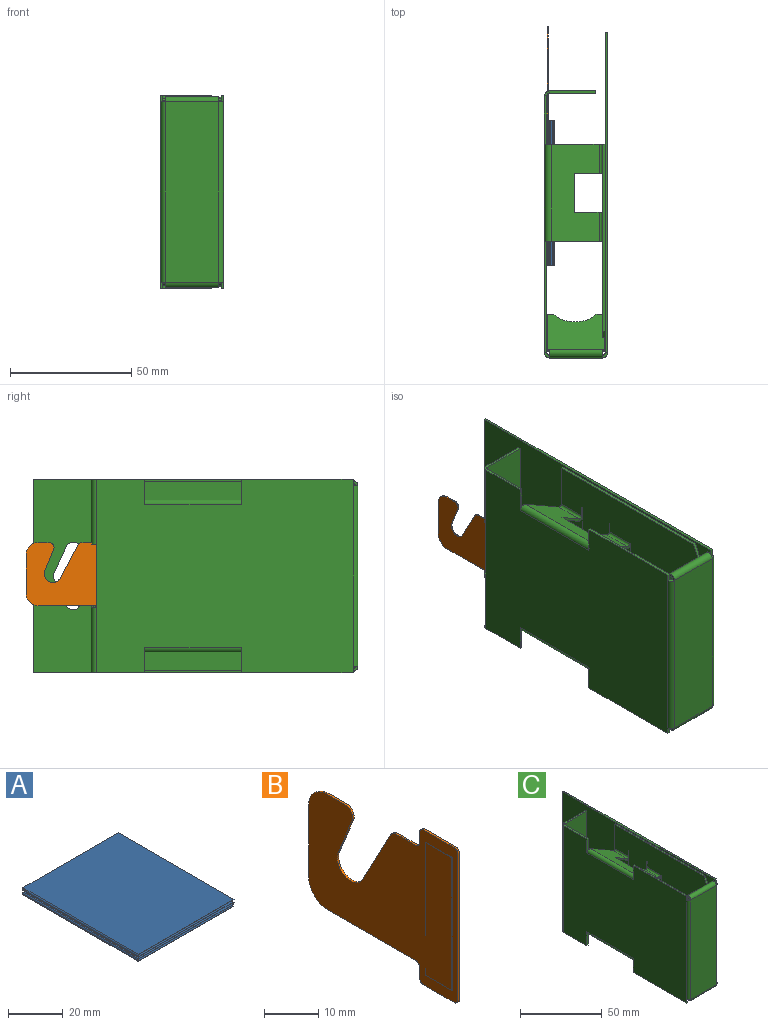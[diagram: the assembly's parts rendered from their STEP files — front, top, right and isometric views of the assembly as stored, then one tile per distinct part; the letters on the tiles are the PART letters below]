
ASSEMBLY  parts=3 mates=2
PART A: 54 faces, bbox 50x60x3.1 mm
  f0: plane 60x0.1mm, normal (1,0,0), area 6mm2, adj f1,f2,f3,f4
  f1: plane 49.5x0.1mm, normal (0,1,0), area 4.9mm2, adj f0,f3,f4,f10
  f2: plane 49.5x0.1mm, normal (0,-1,0), area 4.9mm2, adj f0,f3,f4,f9
  f3: plane 60x49.5mm, normal (0,0,1), area 2970mm2, adj f0,f1,f2,f11
  f4: plane 60x49.5mm, normal (0,0,-1), area 2970mm2, adj f0,f1,f2,f12
  f5: plane 0.1x0.1mm, normal (0,1,0), area 0mm2, adj f7,f8,f10,f14
  f6: plane 0.1x0.1mm, normal (0,-1,0), area 0mm2, adj f7,f8,f9,f13
  f7: plane 60x0.1mm, normal (-1,0,0), area 6mm2, adj f5,f6,f11,f15
  f8: plane 60x0.1mm, normal (1,0,0), area 6mm2, adj f5,f6,f12,f16
  f9: plane 0.5x0.5mm, normal (0,-1,0), area 0.1mm2, adj f2,f6,f11,f12
  f10: plane 0.5x0.5mm, normal (0,1,0), area 0.1mm2, adj f1,f5,f11,f12
  f11: cylinder r=0.5mm len=60mm, axis (0,-1,0), area 47.1mm2, adj f3,f7,f9,f10
  f12: cylinder r=0.4mm len=60mm, axis (0,-1,0), area 37.7mm2, adj f4,f8,f9,f10
  f13: plane 0.5x0.5mm, normal (0,-1,0), area 0.1mm2, adj f6,f15,f16,f18
  f14: plane 0.5x0.5mm, normal (0,1,0), area 0.1mm2, adj f5,f15,f16,f17
  f15: cylinder r=0.5mm len=60mm, axis (0,-1,0), area 47.1mm2, adj f7,f13,f14,f19
  f16: cylinder r=0.4mm len=60mm, axis (0,-1,0), area 37.7mm2, adj f8,f13,f14,f20
  f17: plane 49x0.1mm, normal (0,1,0), area 4.9mm2, adj f14,f19,f20,f29
  f18: plane 49x0.1mm, normal (0,-1,0), area 4.9mm2, adj f13,f19,f20,f30
  f19: plane 60x49mm, normal (0,0,-1), area 2940mm2, adj f15,f17,f18,f32
  f20: plane 60x49mm, normal (0,0,1), area 2940mm2, adj f16,f17,f18,f31
  f21: plane 0.5x0.5mm, normal (0,1,0), area 0.1mm2, adj f23,f24,f25,f33
  f22: plane 0.5x0.5mm, normal (0,-1,0), area 0.1mm2, adj f23,f24,f26,f34
  f23: cylinder r=0.5mm len=60mm, axis (0,1,0), area 47.1mm2, adj f21,f22,f28,f36
  f24: cylinder r=0.4mm len=60mm, axis (0,1,0), area 37.7mm2, adj f21,f22,f27,f35
  f25: plane 0.1x0.1mm, normal (0,1,0), area 0mm2, adj f21,f27,f28,f29
  f26: plane 0.1x0.1mm, normal (0,-1,0), area 0mm2, adj f22,f27,f28,f30
  f27: plane 60x0.1mm, normal (-1,0,0), area 6mm2, adj f24,f25,f26,f32
  f28: plane 60x0.1mm, normal (1,0,0), area 6mm2, adj f23,f25,f26,f31
  f29: plane 0.5x0.5mm, normal (0,1,0), area 0.1mm2, adj f17,f25,f31,f32
  f30: plane 0.5x0.5mm, normal (0,-1,0), area 0.1mm2, adj f18,f26,f31,f32
  f31: cylinder r=0.5mm len=60mm, axis (0,1,0), area 47.1mm2, adj f20,f28,f29,f30
  f32: cylinder r=0.4mm len=60mm, axis (0,1,0), area 37.7mm2, adj f19,f27,f29,f30
  f33: plane 48.9x0.1mm, normal (0,1,0), area 4.9mm2, adj f21,f35,f36,f46
  f34: plane 48.9x0.1mm, normal (0,-1,0), area 4.9mm2, adj f22,f35,f36,f45
  f35: plane 60x48.9mm, normal (0,0,1), area 2934mm2, adj f24,f33,f34,f47
  f36: plane 60x48.9mm, normal (0,0,-1), area 2934mm2, adj f23,f33,f34,f48
  f37: plane 0.1x0.1mm, normal (0,1,0), area 0mm2, adj f39,f40,f41,f46
  f38: plane 0.1x0.1mm, normal (0,-1,0), area 0mm2, adj f39,f40,f42,f45
  f39: plane 60x0.1mm, normal (-1,0,0), area 6mm2, adj f37,f38,f43,f47
  f40: plane 60x0.1mm, normal (1,0,0), area 6mm2, adj f37,f38,f44,f48
  f41: plane 0.5x0.5mm, normal (0,1,0), area 0.1mm2, adj f37,f43,f44,f49
  f42: plane 0.5x0.5mm, normal (0,-1,0), area 0.1mm2, adj f38,f43,f44,f51
  f43: cylinder r=0.5mm len=60mm, axis (0,1,0), area 47.1mm2, adj f39,f41,f42,f52
  f44: cylinder r=0.4mm len=60mm, axis (0,1,0), area 37.7mm2, adj f40,f41,f42,f53
  f45: plane 0.5x0.5mm, normal (0,-1,0), area 0.1mm2, adj f34,f38,f47,f48
  f46: plane 0.5x0.5mm, normal (0,1,0), area 0.1mm2, adj f33,f37,f47,f48
  f47: cylinder r=0.5mm len=60mm, axis (0,-1,0), area 47.1mm2, adj f35,f39,f45,f46
  f48: cylinder r=0.4mm len=60mm, axis (0,-1,0), area 37.7mm2, adj f36,f40,f45,f46
  f49: plane 49.3x0.1mm, normal (0,1,0), area 4.9mm2, adj f41,f50,f52,f53
  f50: plane 60x0.1mm, normal (1,0,0), area 6mm2, adj f49,f51,f52,f53
  f51: plane 49.3x0.1mm, normal (0,-1,0), area 4.9mm2, adj f42,f50,f52,f53
  f52: plane 60x49.3mm, normal (0,0,-1), area 2958mm2, adj f43,f49,f50,f51
  f53: plane 60x49.3mm, normal (0,0,1), area 2958mm2, adj f44,f49,f50,f51
PART B: 29 faces, bbox 0.5x39x35 mm
  f0: plane 4.51x0.4mm, normal (0,0,1), area 1.8mm2, adj f1,f2,f25,f28
  f1: plane 39x35mm, normal (-1,0,0), area 750.1mm2, adj f0,f3,f4,f5,f6,f7,f8,f9
  f2: plane 39x35mm, normal (1,0,0), area 960.1mm2, adj f0,f3,f4,f5,f6,f7,f8,f9
  f3: plane 4.94x0.4mm, normal (0,0,1), area 2mm2, adj f1,f2,f11,f26
  f4: plane 2.5x0.4mm, normal (0,1,0), area 1mm2, adj f1,f2,f11,f16
  f5: plane 8x0.4mm, normal (0,0,1), area 3.2mm2, adj f1,f2,f13,f16
  f6: plane 33x0.4mm, normal (0,-1,0), area 13.2mm2, adj f1,f2,f13,f14
  f7: plane 8x0.4mm, normal (0,0,-1), area 3.2mm2, adj f1,f2,f14,f15
  f8: plane 2.5x0.4mm, normal (0,1,0), area 1mm2, adj f1,f2,f12,f15
  f9: plane 23x0.4mm, normal (0,0,-1), area 9.2mm2, adj f1,f2,f12,f27
  f10: plane 16x0.4mm, normal (0,1,0), area 6.4mm2, adj f1,f2,f27,f28
  f11: cylinder r=1mm len=1mm, axis (1,0,0), area 0.6mm2, adj f1,f2,f3,f4
  f12: cylinder r=1mm len=1mm, axis (-1,0,0), area 0.6mm2, adj f1,f2,f8,f9
  f13: cylinder r=1mm len=1mm, axis (1,0,0), area 0.6mm2, adj f1,f2,f5,f6
  f14: cylinder r=1mm len=1mm, axis (-1,0,0), area 0.6mm2, adj f1,f2,f6,f7
  f15: cylinder r=1mm len=1mm, axis (1,0,0), area 0.6mm2, adj f1,f2,f7,f8
  f16: cylinder r=1mm len=1mm, axis (-1,0,0), area 0.6mm2, adj f1,f2,f4,f5
  f17: plane 30x0.1mm, normal (0,1,0), area 3mm2, adj f1,f18,f20,f21
  f18: plane 7x0.1mm, normal (0,0,1), area 0.7mm2, adj f1,f17,f19,f21
  f19: plane 30x0.1mm, normal (0,-1,0), area 3mm2, adj f1,f18,f20,f21
  f20: plane 7x0.1mm, normal (0,0,-1), area 0.7mm2, adj f1,f17,f19,f21
  f21: plane 30x7mm, normal (-1,0,0), area 210mm2, adj f17,f18,f19,f20
  f22: plane 8.94x3.61mm, normal (0,-0.93,-0.37), area 3.9mm2, adj f1,f2,f24,f25
  f23: plane 13.25x7.05mm, normal (0,0.88,0.47), area 6mm2, adj f1,f2,f24,f26
  f24: cylinder r=3.5mm len=6.75mm, axis (1,0,0), area 4.4mm2, adj f1,f2,f22,f23
  f25: cylinder r=2mm len=2.75mm, axis (1,0,0), area 1.6mm2, adj f0,f1,f2,f22
  f26: cylinder r=2mm len=1.77mm, axis (1,0,0), area 0.9mm2, adj f1,f2,f3,f23
  f27: cylinder r=5mm len=5mm, axis (1,0,0), area 3.1mm2, adj f1,f2,f9,f10
  f28: cylinder r=5mm len=5mm, axis (-1,0,0), area 3.1mm2, adj f0,f1,f2,f10
PART C: 153 faces, bbox 26x134x80 mm
  f0: plane 2.75x1mm, normal (0,-1,0), area 2.7mm2, adj f4,f11,f12,f121
  f1: plane 20x1mm, normal (0,0,-1), area 20mm2, adj f2,f11,f12,f23
  f2: plane 10.46x1mm, normal (0,-1,0), area 9.2mm2, adj f1,f11,f12,f115
  f3: plane 10.46x1mm, normal (0,1,0), area 9.2mm2, adj f4,f11,f12,f115
  f4: plane 46x1mm, normal (0,0,-1), area 46mm2, adj f0,f3,f11,f12
  f5: plane 2.75x1mm, normal (0,-1,0), area 2.7mm2, adj f6,f11,f12,f122
  f6: plane 46x1mm, normal (0,0,1), area 46mm2, adj f5,f7,f11,f12
  f7: plane 10.46x1mm, normal (0,1,0), area 9.2mm2, adj f6,f11,f12,f79
  f8: plane 10.46x1mm, normal (0,-1,0), area 9.2mm2, adj f9,f11,f12,f79
  f9: plane 20x1mm, normal (0,0,1), area 20mm2, adj f8,f11,f12,f20
  f10: plane 26x1mm, normal (0,1,0), area 26mm2, adj f11,f12,f19,f24
  f11: plane 106x80mm, normal (-1,0,0), area 7642.9mm2, adj f0,f1,f2,f3,f4,f5,f6,f7
  f12: plane 106x80mm, normal (1,0,0), area 7642.9mm2, adj f0,f1,f2,f3,f4,f5,f6,f7
  f13: plane 19x1mm, normal (0,0,1), area 19mm2, adj f14,f17,f18,f20
  f14: plane 80x1mm, normal (1,0,0), area 80mm2, adj f13,f15,f17,f18
  f15: plane 19x1mm, normal (0,0,-1), area 19mm2, adj f14,f17,f18,f23
  f16: plane 26x1mm, normal (-1,0,0), area 26mm2, adj f17,f18,f19,f24
  f17: plane 80x19mm, normal (0,1,0), area 1520mm2, adj f13,f14,f15,f16,f21,f25
  f18: plane 80x19mm, normal (0,-1,0), area 1520mm2, adj f13,f14,f15,f16,f22,f26
  f19: plane 2x2mm, normal (0,0,-1), area 2.4mm2, adj f10,f16,f21,f22
  f20: plane 2x2mm, normal (0,0,1), area 2.4mm2, adj f9,f13,f21,f22
  f21: cylinder r=2mm len=27mm, axis (0,0,-1), area 84.8mm2, adj f11,f17,f19,f20
  f22: cylinder r=1mm len=27mm, axis (0,0,-1), area 42.4mm2, adj f12,f18,f19,f20
  f23: plane 2x2mm, normal (0,0,-1), area 2.4mm2, adj f1,f15,f25,f26
  f24: plane 2x2mm, normal (0,0,1), area 2.4mm2, adj f10,f16,f25,f26
  f25: cylinder r=2mm len=27mm, axis (0,0,-1), area 84.8mm2, adj f11,f17,f23,f24
  f26: cylinder r=1mm len=27mm, axis (0,0,-1), area 42.4mm2, adj f12,f18,f23,f24
  f27: plane 2x2mm, normal (0,-1,0), area 1.9mm2, adj f12,f65,f79,f80
  f28: plane 2x2mm, normal (0,1,0), area 1.9mm2, adj f12,f64,f79,f80
  f29: plane 2x2mm, normal (0,1,0), area 1.9mm2, adj f12,f104,f115,f116
  f30: plane 2x2mm, normal (0,-1,0), area 1.9mm2, adj f12,f103,f115,f116
  f31: plane 2.75x1mm, normal (0,-1,0), area 2.7mm2, adj f32,f42,f43,f118
  f32: plane 132x1mm, normal (0,0,1), area 132mm2, adj f31,f41,f42,f43
  f33: plane 2.75x1mm, normal (0,-1,0), area 2.7mm2, adj f34,f42,f43,f117
  f34: plane 132x1mm, normal (0,0,-1), area 132mm2, adj f33,f41,f42,f43
  f35: cylinder r=3mm len=5.73mm, axis (1,0,0), area 8.1mm2, adj f36,f40,f42,f43
  f36: plane 11x5mm, normal (0,-0.91,-0.41), area 12.1mm2, adj f35,f37,f42,f43
  f37: cylinder r=3mm len=2.48mm, axis (1,0,0), area 2.6mm2, adj f36,f38,f42,f43
  f38: plane 11x5mm, normal (0,-0.91,0.41), area 12.1mm2, adj f37,f39,f42,f43
  f39: cylinder r=3mm len=5.73mm, axis (1,0,0), area 8.1mm2, adj f38,f40,f42,f43
  f40: plane 22x1mm, normal (0,1,0), area 22mm2, adj f35,f39,f42,f43
  f41: plane 80x1mm, normal (0,1,0), area 80mm2, adj f32,f34,f42,f43
  f42: plane 132x80mm, normal (1,0,0), area 10338.2mm2, adj f31,f32,f33,f34,f35,f36,f37,f38
  f43: plane 132x80mm, normal (-1,0,0), area 6121mm2, adj f31,f32,f33,f34,f35,f36,f37,f38
  f44: plane 18.12x1mm, normal (0,1,0), area 18.1mm2, adj f43,f61,f62,f76
  f45: plane 4.12x1mm, normal (0,-1,0), area 4.1mm2, adj f43,f46,f62,f75
  f46: plane 1x0.2mm, normal (0,0,-1), area 0.2mm2, adj f43,f45,f47,f62
  f47: plane 28x1mm, normal (0,1,0), area 28mm2, adj f43,f46,f48,f62
  f48: plane 5.2x1mm, normal (0,0,-1), area 5.2mm2, adj f43,f47,f49,f62
  f49: plane 6.1x1.73mm, normal (0,-0.96,0.27), area 6.3mm2, adj f43,f48,f50,f62
  f50: plane 8.66x1mm, normal (0,0,-1), area 8.7mm2, adj f43,f49,f51,f62
  f51: plane 6.1x1.73mm, normal (0,0.96,0.27), area 6.3mm2, adj f43,f50,f52,f62
  f52: plane 5.2x1mm, normal (0,0,-1), area 5.2mm2, adj f43,f51,f53,f62
  f53: plane 28x1mm, normal (0,-1,0), area 28mm2, adj f43,f52,f54,f62
  f54: plane 1x0.2mm, normal (0,0,-1), area 0.2mm2, adj f43,f53,f55,f62
  f55: plane 4.12x1mm, normal (0,1,0), area 4.1mm2, adj f43,f54,f62,f72
  f56: plane 1x0.1mm, normal (0,0,-1), area 0.1mm2, adj f43,f57,f62,f71
  f57: plane 17.88x1mm, normal (0,1,0), area 17.9mm2, adj f43,f56,f58,f62
  f58: plane 21.5x1mm, normal (0,0,-1), area 21.5mm2, adj f43,f57,f59,f62
  f59: plane 9.11x1mm, normal (0,-1,0), area 9.1mm2, adj f43,f58,f60,f62
  f60: plane 21.52x18.06mm, normal (0,-0.77,-0.64), area 28.1mm2, adj f43,f59,f62,f63
  f61: plane 77.16x1mm, normal (0,0,1), area 77.2mm2, adj f43,f44,f62,f63
  f62: plane 79.66x42mm, normal (-1,0,0), area 2113.8mm2, adj f44,f45,f46,f47,f48,f49,f50,f51
  f63: plane 5.36x2.5mm, normal (0,-0.91,0.42), area 5.9mm2, adj f43,f60,f61,f62
  f64: plane 20x12.12mm, normal (0,1,0), area 22.5mm2, adj f28,f69,f70,f76
  f65: plane 20x12.12mm, normal (0,-1,0), area 22.5mm2, adj f27,f69,f70,f71
  f66: plane 10.64x6.72mm, normal (0,1,0), area 11.7mm2, adj f67,f69,f70,f72
  f67: plane 16x0.87mm, normal (0.87,0,-0.5), area 16mm2, adj f66,f68,f69,f70
  f68: plane 10.64x6.72mm, normal (0,-1,0), area 11.7mm2, adj f67,f69,f70,f75
  f69: plane 40x19.5mm, normal (0.5,0,0.87), area 713.3mm2, adj f64,f65,f66,f67,f68,f74,f78,f79
  f70: plane 40x19.5mm, normal (-0.5,0,-0.87), area 713.3mm2, adj f64,f65,f66,f67,f68,f73,f77,f80
  f71: plane 3x2mm, normal (0,-1,0), area 3.1mm2, adj f56,f65,f73,f74
  f72: plane 3x2mm, normal (0,1,0), area 3.1mm2, adj f55,f66,f73,f74
  f73: cylinder r=2mm len=12mm, axis (0,-1,0), area 50.3mm2, adj f43,f70,f71,f72
  f74: cylinder r=1mm len=12mm, axis (0,-1,0), area 25.1mm2, adj f62,f69,f71,f72
  f75: plane 3x2mm, normal (0,-1,0), area 3.1mm2, adj f45,f68,f77,f78
  f76: plane 3x2mm, normal (0,1,0), area 3.1mm2, adj f44,f64,f77,f78
  f77: cylinder r=2mm len=12mm, axis (0,-1,0), area 50.3mm2, adj f43,f70,f75,f76
  f78: cylinder r=1mm len=12mm, axis (0,-1,0), area 25.1mm2, adj f62,f69,f75,f76
  f79: cylinder r=2mm len=40mm, axis (0,-1,0), area 167.6mm2, adj f7,f8,f11,f27,f28,f69
  f80: cylinder r=1mm len=40mm, axis (0,-1,0), area 83.8mm2, adj f12,f27,f28,f70
  f81: plane 21.52x18.06mm, normal (0,-0.77,0.64), area 28.1mm2, adj f43,f82,f98,f99
  f82: plane 9.11x1mm, normal (0,-1,0), area 9.1mm2, adj f43,f81,f83,f98
  f83: plane 21.6x1mm, normal (0,0,1), area 21.6mm2, adj f43,f82,f84,f98
  f84: plane 17.88x1mm, normal (0,1,0), area 16.6mm2, adj f43,f83,f98,f109
  f85: plane 4.12x1mm, normal (0,1,0), area 4.1mm2, adj f43,f86,f98,f108
  f86: plane 1x0.2mm, normal (0,0,1), area 0.2mm2, adj f43,f85,f87,f98
  f87: plane 21.9x1mm, normal (0,-1,0), area 21.9mm2, adj f43,f86,f88,f98
  f88: plane 5.33x1mm, normal (0,0,1), area 5.3mm2, adj f43,f87,f89,f98
  f89: plane 6.1x1.73mm, normal (0,-0.96,-0.27), area 6.3mm2, adj f43,f88,f90,f98
  f90: plane 8.4x1mm, normal (0,0,1), area 8.4mm2, adj f43,f89,f91,f98
  f91: plane 6.1x1.73mm, normal (0,0.96,-0.27), area 6.3mm2, adj f43,f90,f92,f98
  f92: plane 5.33x1mm, normal (0,0,1), area 5.3mm2, adj f43,f91,f93,f98
  f93: plane 21.9x1mm, normal (0,1,0), area 21.9mm2, adj f43,f92,f94,f98
  f94: plane 1x0.2mm, normal (0,0,1), area 0.2mm2, adj f43,f93,f95,f98
  f95: plane 4.12x1mm, normal (0,-1,0), area 4.1mm2, adj f43,f94,f98,f112
  f96: plane 18.12x1mm, normal (0,1,0), area 18.1mm2, adj f43,f97,f98,f111
  f97: plane 77.16x1mm, normal (0,0,-1), area 77.2mm2, adj f43,f96,f98,f99
  f98: plane 79.66x42mm, normal (-1,0,0), area 2103.4mm2, adj f81,f82,f83,f84,f85,f86,f87,f88
  f99: plane 5.36x2.5mm, normal (0,-0.91,-0.42), area 5.9mm2, adj f43,f81,f97,f98
  f100: plane 2x2mm, normal (0,-1,0), area 1.9mm2, adj f98,f103,f109,f110
  f101: plane 16x0.87mm, normal (0.87,0,0.5), area 16mm2, adj f102,f105,f106,f107
  f102: plane 10.64x6.72mm, normal (0,1,0), area 11.7mm2, adj f101,f106,f107,f108
  f103: plane 20x12.12mm, normal (0,-1,0), area 22.5mm2, adj f30,f100,f106,f107
  f104: plane 20x12.12mm, normal (0,1,0), area 22.5mm2, adj f29,f106,f107,f111
  f105: plane 10.64x6.72mm, normal (0,-1,0), area 11.7mm2, adj f101,f106,f107,f112
  f106: plane 40x19.5mm, normal (0.5,0,-0.87), area 713.3mm2, adj f101,f102,f103,f104,f105,f110,f114,f115
  f107: plane 40x19.5mm, normal (-0.5,0,0.87), area 713.3mm2, adj f101,f102,f103,f104,f105,f109,f113,f116
  f108: plane 3x2mm, normal (0,1,0), area 3.1mm2, adj f85,f102,f109,f110
  f109: cylinder r=2mm len=12mm, axis (0,1,0), area 50.3mm2, adj f43,f84,f100,f107,f108
  f110: cylinder r=1mm len=12mm, axis (0,1,0), area 25.1mm2, adj f98,f100,f106,f108
  f111: plane 3x2mm, normal (0,1,0), area 3.1mm2, adj f96,f104,f113,f114
  f112: plane 3x2mm, normal (0,-1,0), area 3.1mm2, adj f95,f105,f113,f114
  f113: cylinder r=2mm len=12mm, axis (0,1,0), area 50.3mm2, adj f43,f107,f111,f112
  f114: cylinder r=1mm len=12mm, axis (0,1,0), area 25.1mm2, adj f98,f106,f111,f112
  f115: cylinder r=2mm len=40mm, axis (0,1,0), area 167.6mm2, adj f2,f3,f11,f29,f30,f106
  f116: cylinder r=1mm len=40mm, axis (0,1,0), area 83.8mm2, adj f12,f29,f30,f107
  f117: plane 2x2mm, normal (0,0,-1), area 2.4mm2, adj f33,f119,f120,f136
  f118: plane 2x2mm, normal (0,0,1), area 2.4mm2, adj f31,f119,f120,f150
  f119: cylinder r=2mm len=74.51mm, axis (0,0,-1), area 234.1mm2, adj f42,f117,f118,f125
  f120: cylinder r=1mm len=74.51mm, axis (0,0,-1), area 117mm2, adj f43,f117,f118,f126
  f121: plane 2x2mm, normal (0,0,-1), area 2.4mm2, adj f0,f123,f124,f137
  f122: plane 2x2mm, normal (0,0,1), area 2.4mm2, adj f5,f123,f124,f149
  f123: cylinder r=2mm len=74.51mm, axis (0,0,-1), area 234.1mm2, adj f11,f121,f122,f125
  f124: cylinder r=1mm len=74.51mm, axis (0,0,-1), area 117mm2, adj f12,f121,f122,f126
  f125: plane 74.51x22mm, normal (0,-1,0), area 1639.1mm2, adj f119,f123,f138,f151
  f126: plane 74.51x22mm, normal (0,1,0), area 1639.1mm2, adj f120,f124,f139,f152
  f127: plane 3.69x0.77mm, normal (0,0.64,0.77), area 3.7mm2, adj f128,f133,f134,f135
  f128: plane 17.88x15.23mm, normal (1,0,0), area 22.5mm2, adj f127,f129,f134,f135
  f129: plane 0.9x0.77mm, normal (0,-0.64,-0.77), area 0.9mm2, adj f128,f134,f135,f136
  f130: plane 0.9x0.77mm, normal (0,-0.64,-0.77), area 0.9mm2, adj f131,f134,f135,f137
  f131: plane 17.88x15.23mm, normal (-1,0,0), area 22.5mm2, adj f130,f132,f134,f135
  f132: plane 2.79x0.77mm, normal (0,0.64,0.77), area 2.8mm2, adj f131,f133,f134,f135
  f133: cylinder r=10mm len=17.32mm, axis (0,0.77,-0.64), area 20.9mm2, adj f127,f132,f134,f135
  f134: plane 23.8x17.24mm, normal (0,0.77,-0.64), area 474.2mm2, adj f127,f128,f129,f130,f131,f132,f133,f138
  f135: plane 23.8x17.24mm, normal (0,-0.77,0.64), area 474.2mm2, adj f127,f128,f129,f130,f131,f132,f133,f139
  f136: plane 3.53x2mm, normal (1,0,0), area 3.7mm2, adj f117,f129,f138,f139
  f137: plane 3.53x2mm, normal (-1,0,0), area 3.7mm2, adj f121,f130,f138,f139
  f138: cylinder r=2mm len=22mm, axis (1,0,0), area 107.5mm2, adj f125,f134,f136,f137
  f139: cylinder r=1mm len=22mm, axis (1,0,0), area 53.8mm2, adj f126,f135,f136,f137
  f140: plane 2.79x0.77mm, normal (0,0.64,-0.77), area 2.8mm2, adj f141,f146,f147,f148
  f141: plane 17.88x15.23mm, normal (-1,0,0), area 22.5mm2, adj f140,f142,f147,f148
  f142: plane 0.9x0.77mm, normal (0,-0.64,0.77), area 0.9mm2, adj f141,f147,f148,f149
  f143: plane 0.9x0.77mm, normal (0,-0.64,0.77), area 0.9mm2, adj f144,f147,f148,f150
  f144: plane 17.88x15.23mm, normal (1,0,0), area 22.5mm2, adj f143,f145,f147,f148
  f145: plane 3.69x0.77mm, normal (0,0.64,-0.77), area 3.7mm2, adj f144,f146,f147,f148
  f146: cylinder r=10mm len=17.32mm, axis (0,0.77,0.64), area 20.9mm2, adj f140,f145,f147,f148
  f147: plane 23.8x17.24mm, normal (0,0.77,0.64), area 474.2mm2, adj f140,f141,f142,f143,f144,f145,f146,f151
  f148: plane 23.8x17.24mm, normal (0,-0.77,-0.64), area 474.2mm2, adj f140,f141,f142,f143,f144,f145,f146,f152
  f149: plane 3.53x2mm, normal (-1,0,0), area 3.7mm2, adj f122,f142,f151,f152
  f150: plane 3.53x2mm, normal (1,0,0), area 3.7mm2, adj f118,f143,f151,f152
  f151: cylinder r=2mm len=22mm, axis (-1,0,0), area 107.5mm2, adj f125,f147,f149,f150
  f152: cylinder r=1mm len=22mm, axis (-1,0,0), area 53.8mm2, adj f126,f148,f149,f150
PLACE A rot(axis=(0.71,0,0.71),180deg) t=(-2.32,23.59,6.59)mm
PLACE B t=(-3.22,14.44,7.56)mm
PLACE C t=(-3.32,15.59,6.79)mm
MATE fastened A.f52 <-> B.f21  axis (1,0,0) through (-2.32,53.59,6.79)mm
MATE fastened B.f21 <-> C.f12  axis (1,0,0) through (-2.32,63.59,6.79)mm
